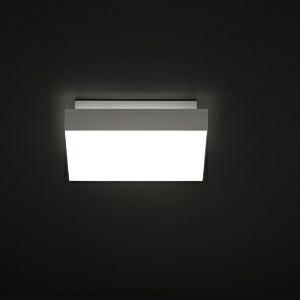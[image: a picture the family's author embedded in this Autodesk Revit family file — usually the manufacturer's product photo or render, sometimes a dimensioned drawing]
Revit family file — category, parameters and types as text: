
# Revit family: spectral_norea_norea-qa_422_5200_840_os_cc5e
name_source: partatom
category: Lighting Fixtures
revit_build: Autodesk Revit 2016 (Build: 20150220_1215(x64)
units: mm (PartAtom-declared; Revit-internal decimal feet)

## family parameters
Cut with Voids When Loaded = No
Host = Face
Light Source = No
Part Type = Normal
Room Calculation Point = No
Round Connector Dimension = Use Diameter
Shared = No

## types (1)
- SPECTRAL NOREA (1 x )
    Apparent Load = 0 VA
    Approval mark = CE
    CIE Flux Codes = 48 78 95 100 61
    Control Gear = Electronic transformer
    Default Elevation = 1800 mm
    Description = SPT0000101
NOREA surface-mounted luminaire

Design:
Square luminaire element comprising an opal acrylic glass panel in a natural anodised aluminium profile frame surround. The frame is suspended at the
metal body. The LED module is formed as a square LED flat board and screwed to the luminaire element. For connection of the luminaire this can be hinged down and fastened with screws at an oblong hole in the powder-coated metal body. The indirect component is ensured by recesses in the top of the metal body. The metal body accommodates the electrical components and electronic ballast. Luminaire with heat-resistant wiring. Homogenous illumination of the light surface. Suitable for ceiling or wall mounting. 
Protection rating IP20, safety class I.

Colour:
Housing - similar to RAL 9016 white silk matt;
Frame - natural anodised
    Height = 80 mm  [stored 0.262467 ft]
    Lamp = 1 x
    Lamp count = 1
    Length = 422 mm
    Luminous efficacy = 0 lm/W
    Manufacturer = Ridi
    ModVariant = No
    Model = NOREA-QA 422/5200/840 OS
    Mounting Place = Ceiling
    Mounting Type = Surface mounted
    Number of Poles = 1
    OnlyDefault = Yes
    Power Factor = 1
    Product Name = SPECTRAL NOREA
    Product group = Ceiling mounted luminaire
    ProductGroupID = 3
    Protection Class = Protection class
    Protection Degree = IP 20
    RlxData = <blob elided: 36053 chars, md5=da0316c3>
    Socket = socket
    Standby Power = 0 W
    System Light Flux = 0 lm
    System Power = 0 W
    Type Image = leuchtstoffklein02_-_kopie.jpg
    URL = http://reluxnet.relux.com
    VarID = 1
    Voltage = 0 V
    Weight = 0.00 kg
    Width = 422 mm

note: [stored X ft] marks values corroborated as IEEE doubles in the binary element streams (Revit-internal decimal feet)

## geometry (parser evidence)
native form markers: Sweep x9
no freeform markers — native parametric forms only
